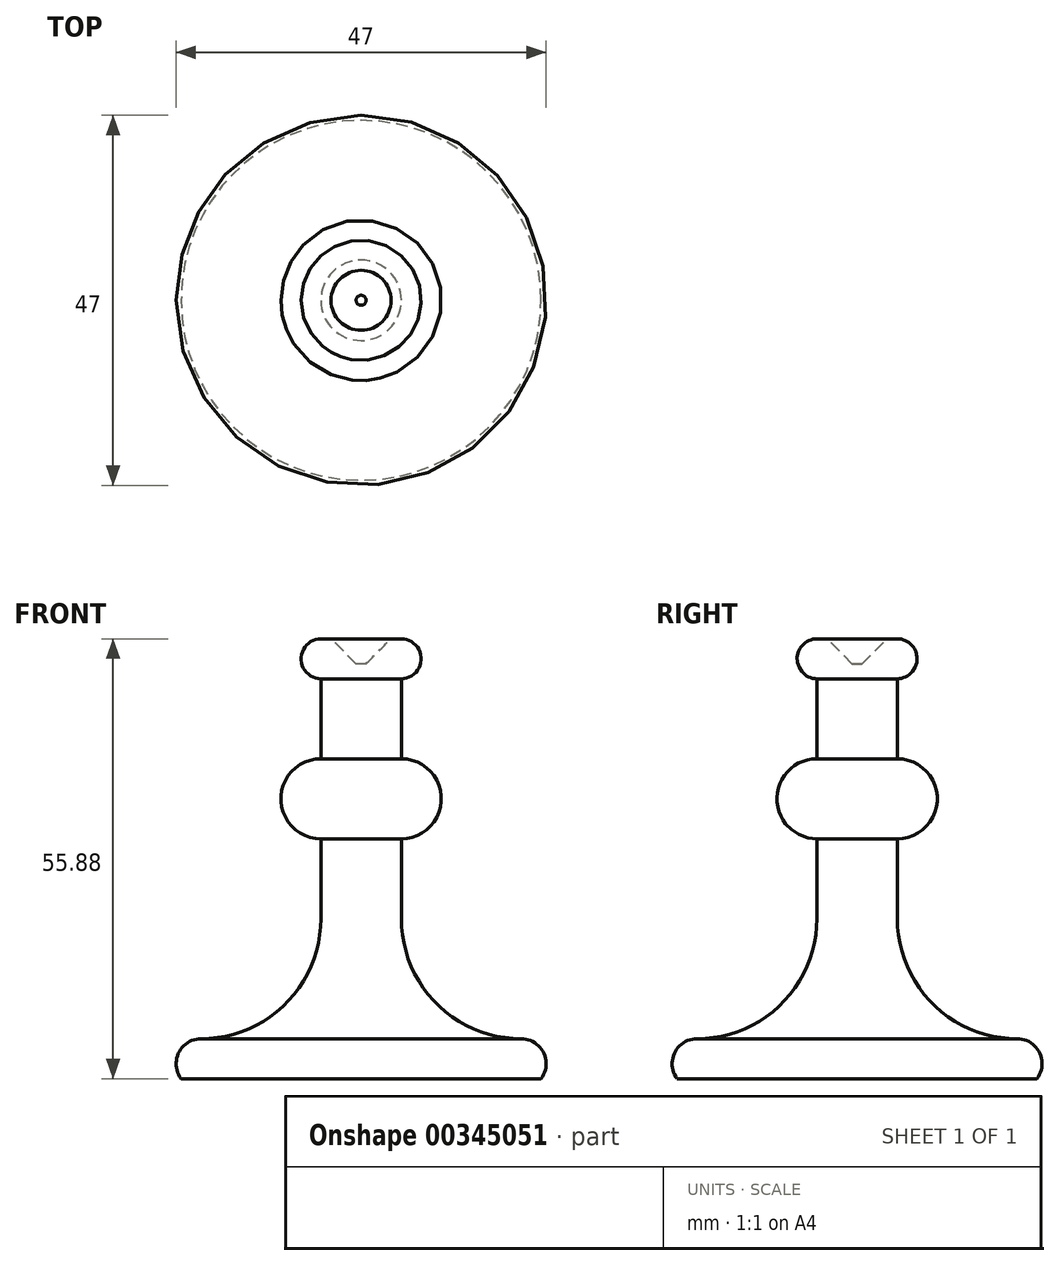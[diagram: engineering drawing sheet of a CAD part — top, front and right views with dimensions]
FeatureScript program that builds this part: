
annotation { "Feature Type Name" : "Feature", "Feature Type Description" : "" }
export const myFeature = defineFeature(function(context is Context, id is Id, definition is map)
    precondition{}
    {
        {
            var Q0;
            Q0=qCreatedBy(makeId("Front.planeOp"),FACE);
            var sketch = newSketch(context, id + "F0", { "sketchPlane" : qUnion([Q0])});
            skLineSegment(sketch, "E0", {"start": v(22.86, 0) * mm, "end": v(0, 0) * mm});
            skLineSegment(sketch, "E1", {"start": v(0, 0) * mm, "end": v(0, 55.88) * mm});
            skLineSegment(sketch, "E2", {"start": v(0, 55.88) * mm, "end": v(5.08, 55.88) * mm});
            skArc(sketch, "E3", {"start": v(5.08, 55.88) * mm, "mid": v(7.62, 53.35) * mm, "end": v(5.1, 50.8) * mm});
            skLineSegment(sketch, "E4", {"start": v(5.1, 50.8) * mm, "end": v(5.1, 40.64) * mm});
            skArc(sketch, "E5", {"start": v(5.1, 30.48) * mm, "mid": v(10.19, 35.56) * mm, "end": v(5.1, 40.64) * mm});
            skLineSegment(sketch, "E6", {"start": v(5.1, 30.48) * mm, "end": v(5.1, 20.32) * mm});
            skArc(sketch, "E7", {"start": v(5.1, 20.32) * mm, "mid": v(9.56, 9.55) * mm, "end": v(20.32, 5.08) * mm});
            skArc(sketch, "E8", {"start": v(20.32, 5.08) * mm, "mid": v(23.16, 3.32) * mm, "end": v(22.86, 0) * mm});
            skSolve(sketch);
        }
        {
            var Q0;
            Q0=makeQuery(id+"F0.imprint","IMPRINT",FACE,{"disambiguationData":[TD([[makeQuery(id+"F0.imprint","IMPRINT",EDGE,{"derivedFrom":sQuery(id+"F0.wireOp",EDGE,"E0")}),-1.0]])]});
            var Q1;
            Q1=sQuery(id+"F0.wireOp",EDGE,"E1");
            revolve(context, id + "F1", {"entities" : qUnion([Q0]), "axis" : qUnion([Q1]), "revolveType" : RevolveType.FULL});
        }
        {
            var Q0;
            Q0=qCreatedBy(makeId("Front.planeOp"),FACE);
            var sketch = newSketch(context, id + "F2", { "sketchPlane" : qUnion([Q0])});
            skEllipse(sketch, "E9", {"center": v(0, 2.54) * mm, "majorRadius": 4.45 * mm, "minorRadius": 1.27 * mm, "majorAxis": v(1, 0)});
            skSolve(sketch);
        }
        {
            var Q0;
            Q0=qCreatedBy(makeId("Right.planeOp"),FACE);
            var sketch = newSketch(context, id + "F3", { "sketchPlane" : qUnion([Q0])});
            skLineSegment(sketch, "E10", {"start": v(0, 2.54) * mm, "end": v(15.24, 2.54) * mm});
            skArc(sketch, "E11", {"start": v(15.24, 2.54) * mm, "mid": v(32.99, 6.92) * mm, "end": v(46.66, 19.05) * mm});
            skArc(sketch, "E12", {"start": v(46.66, 19.05) * mm, "mid": v(42.47, 27.01) * mm, "end": v(38.3, 19.05) * mm});
            skSolve(sketch);
        }
        {
            var Q0;
            Q0=makeQuery(id+"F1.opRevolve","SWEPT_FACE",FACE,{"disambiguationData":[OSD([sQuery(id+"F0.wireOp",EDGE,"E2")])]});
            var sketch = newSketch(context, id + "F4", { "sketchPlane" : qUnion([Q0])});
            skCircle(sketch, "E13", {"center": v(0, 0) * mm, "radius": 3.81 * mm});
            skSolve(sketch);
        }
        {
            var Q0;
            Q0=makeQuery(id+"F4.imprint","IMPRINT",FACE,{"disambiguationData":[TD([[makeQuery(id+"F4.imprint","IMPRINT",EDGE,{"derivedFrom":sQuery(id+"F4.wireOp",EDGE,"E13")}),1.0]])]});
            extrude(context, id + "F5", {"entities" : qUnion([Q0]), "operationType" : NewBodyOperationType.REMOVE, "endBound" : BoundingType.SYMMETRIC, "depth" : 6.35 * mm, "hasDraft" : true, "draftAngle" : 45 * degree, "draftPullDirection" : true});
        }
    });
